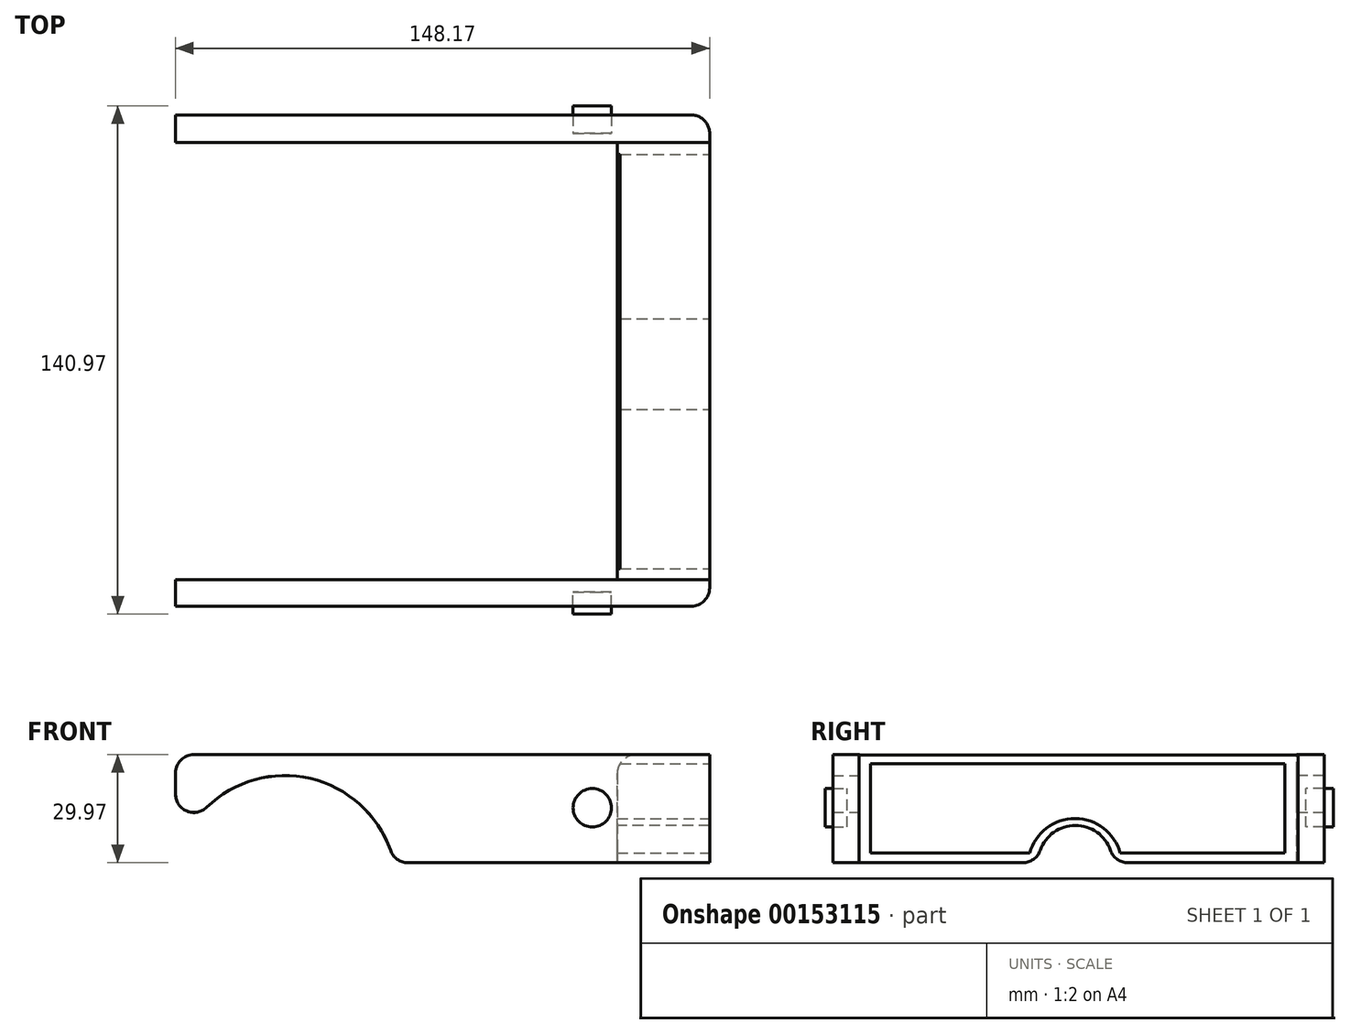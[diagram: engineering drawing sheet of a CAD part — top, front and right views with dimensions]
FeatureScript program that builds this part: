
annotation { "Feature Type Name" : "Feature", "Feature Type Description" : "" }
export const myFeature = defineFeature(function(context is Context, id is Id, definition is map)
    precondition{}
    {
        {
            var Q0;
            Q0=qCreatedBy(makeId("Front.planeOp"),FACE);
            var sketch = newSketch(context, id + "F0", { "sketchPlane" : qUnion([Q0])});
            skLineSegment(sketch, "E0", {"start": v(128.49, 29.97) * mm, "end": v(128.49, 0) * mm});
            skLineSegment(sketch, "E1", {"start": v(-19.65, 0) * mm, "end": v(-19.65, 29.97) * mm});
            skLineSegment(sketch, "E2", {"start": v(-19.65, 29.97) * mm, "end": v(128.49, 29.97) * mm});
            skArc(sketch, "E3", {"start": v(40.96, 0) * mm, "mid": v(10.65, 24.17) * mm, "end": v(-19.65, 0) * mm});
            skLineSegment(sketch, "E4", {"start": v(40.96, 0) * mm, "end": v(128.49, 0) * mm});
            skSolve(sketch);
        }
        {
            var Q0;
            Q0 = qSketchRegion(id + "F0", true);
            extrude(context, id + "F1", {"entities" : qUnion([Q0]), "depth" : 57.53 * mm, "hasSecondDirection" : true, "secondDirectionOppositeDirection" : false, "secondDirectionDepth" : 50.16 * mm});
        }
        {
            var Q0;
            Q0=qCreatedBy(makeId("Right.planeOp"),FACE);
            var sketch = newSketch(context, id + "F2", { "sketchPlane" : qUnion([Q0])});
            skLineSegment(sketch, "E5", {"start": v(-50.22, 29.87) * mm, "end": v(71.57, 29.87) * mm});
            skLineSegment(sketch, "E6", {"start": v(71.57, 29.87) * mm, "end": v(71.57, 0) * mm});
            skLineSegment(sketch, "E7", {"start": v(-50.22, 29.87) * mm, "end": v(-50.22, 0) * mm});
            skLineSegment(sketch, "E8", {"start": v(-50.22, 0) * mm, "end": v(-0.6, 0) * mm});
            skLineSegment(sketch, "E9", {"start": v(71.57, 0) * mm, "end": v(20.08, 0) * mm});
            skArc(sketch, "E10", {"start": v(20.08, 0) * mm, "mid": v(9.74, 10.34) * mm, "end": v(-0.6, 0) * mm});
            skSolve(sketch);
        }
        {
            var Q0;
            Q0 = qSketchRegion(id + "F2", true);
            extrude(context, id + "F3", {"entities" : qUnion([Q0]), "operationType" : NewBodyOperationType.ADD, "depth" : 128.52 * mm, "hasSecondDirection" : true, "secondDirectionOppositeDirection" : false, "secondDirectionDepth" : 102.87 * mm});
        }
        {
            var Q0;
            Q0=qCreatedBy(makeId("Right.planeOp"),FACE);
            var sketch = newSketch(context, id + "F4", { "sketchPlane" : qUnion([Q0])});
            skLineSegment(sketch, "E11", {"start": v(-47.14, 27.49) * mm, "end": v(-47.14, 2.64) * mm});
            skLineSegment(sketch, "E12", {"start": v(-47.14, 2.64) * mm, "end": v(-2.9, 2.64) * mm});
            skLineSegment(sketch, "E13", {"start": v(-47.14, 27.49) * mm, "end": v(67.8, 27.49) * mm});
            skLineSegment(sketch, "E14", {"start": v(67.8, 27.49) * mm, "end": v(67.8, 2.64) * mm});
            skLineSegment(sketch, "E15", {"start": v(67.8, 2.64) * mm, "end": v(22.17, 2.64) * mm});
            skArc(sketch, "E16", {"start": v(22.17, 2.64) * mm, "mid": v(9.63, 12.26) * mm, "end": v(-2.9, 2.64) * mm});
            skSolve(sketch);
        }
        {
            var Q0;
            Q0 = qSketchRegion(id + "F4", true);
            extrude(context, id + "F5", {"entities" : qUnion([Q0]), "operationType" : NewBodyOperationType.REMOVE, "oppositeDirection" : true, "depth" : 156.84 * mm, "hasSecondDirection" : true, "secondDirectionOppositeDirection" : false, "secondDirectionDepth" : 153.67 * mm});
        }
        {
            var Q0;
            Q0=makeQuery(id+"F1.opExtrude","CAP_FACE",FACE,{"disambiguationData":[OSD([sQuery(id+"F0.wireOp",EDGE,"t2ablPFP-ZTGi-keRe-My67-G8U3jhICAmQZ"),sQuery(id+"F0.wireOp",EDGE,"E0"),sQuery(id+"F0.wireOp",EDGE,"AoyKm1Ku-ZIaB-Dyan-j7dL-eiOp278ySbaL"),sQuery(id+"F0.wireOp",EDGE,"k48o5jMi-lDpC-vDEB-Jfvg-DJJhGkoViYC2"),sQuery(id+"F0.wireOp",EDGE,"NTX02WsM-8lT9-VH5H-J8AH-7PksFvNlZK1f")])],"isStart":true});
            var sketch = newSketch(context, id + "F6", { "sketchPlane" : qUnion([Q0])});
            skArc(sketch, "E17", {"start": v(19.65, 0) * mm, "mid": v(-10.65, 24.15) * mm, "end": v(-40.96, 0) * mm});
            skLineSegment(sketch, "E18", {"start": v(-40.96, 0) * mm, "end": v(-128.43, 0) * mm});
            skLineSegment(sketch, "E19", {"start": v(-128.43, 0) * mm, "end": v(-128.49, 29.97) * mm});
            skLineSegment(sketch, "E20", {"start": v(-128.49, 29.97) * mm, "end": v(19.65, 29.97) * mm});
            skLineSegment(sketch, "E21", {"start": v(19.65, 29.97) * mm, "end": v(19.65, 0) * mm});
            skSolve(sketch);
        }
        {
            var Q0;
            Q0 = qSketchRegion(id + "F6", true);
            extrude(context, id + "F7", {"entities" : qUnion([Q0]), "operationType" : NewBodyOperationType.ADD, "depth" : 128.9 * mm, "hasSecondDirection" : true, "secondDirectionOppositeDirection" : false, "secondDirectionDepth" : 121.28 * mm});
        }
        {
            var Q0;
            Q0=makeQuery(id+"F1.opExtrude","CAP_FACE",FACE,{"disambiguationData":[OSD([sQuery(id+"F0.wireOp",EDGE,"t2ablPFP-ZTGi-keRe-My67-G8U3jhICAmQZ"),sQuery(id+"F0.wireOp",EDGE,"E0"),sQuery(id+"F0.wireOp",EDGE,"AoyKm1Ku-ZIaB-Dyan-j7dL-eiOp278ySbaL"),sQuery(id+"F0.wireOp",EDGE,"k48o5jMi-lDpC-vDEB-Jfvg-DJJhGkoViYC2"),sQuery(id+"F0.wireOp",EDGE,"NTX02WsM-8lT9-VH5H-J8AH-7PksFvNlZK1f")])],"isStart":false});
            var sketch = newSketch(context, id + "F8", { "sketchPlane" : qUnion([Q0])});
            skCircle(sketch, "E22", {"center": v(95.95, 15.21) * mm, "radius": 5.33 * mm});
            skSolve(sketch);
        }
        {
            var Q0;
            Q0 = qSketchRegion(id + "F8", true);
            extrude(context, id + "F9", {"entities" : qUnion([Q0]), "depth" : 2.16 * mm, "hasSecondDirection" : true, "secondDirectionOppositeDirection" : true, "secondDirectionDepth" : 3.94 * mm});
        }
        {
            var Q0;
            Q0=makeQuery(id+"F9.opExtrude","CAP_FACE",FACE,{"disambiguationData":[OSD([sQuery(id+"F8.wireOp",EDGE,"E22")])],"isStart":false});
            var sketch = newSketch(context, id + "F10", { "sketchPlane" : qUnion([Q0])});
            skCircle(sketch, "E23", {"center": v(95.95, 15.21) * mm, "radius": 5.34 * mm});
            skSolve(sketch);
        }
        {
            var Q0;
            Q0 = qSketchRegion(id + "F10", true);
            extrude(context, id + "F11", {"entities" : qUnion([Q0]), "oppositeDirection" : true, "depth" : 140.97 * mm, "hasSecondDirection" : true, "secondDirectionOppositeDirection" : true, "secondDirectionDepth" : 133.35 * mm});
        }
        {
            var Q0;
            Q0=makeQuery(id+"F1.opExtrude","SWEPT_EDGE",EDGE,{"disambiguationData":[OSD([sQuery(id+"F0.wireOp",EDGE,"E1"),sQuery(id+"F0.wireOp",EDGE,"E3")])]});
            var Q1;
            Q1=makeQuery(id+"F7.opExtrude","SWEPT_EDGE",EDGE,{"disambiguationData":[OSD([sQuery(id+"F0.wireOp",EDGE,"E3"),sQuery(id+"F6.wireOp",EDGE,"E17"),sQuery(id+"F6.wireOp",EDGE,"E21")])]});
            var Q2;
            Q2=makeQuery(id+"F1.opExtrude","SWEPT_EDGE",EDGE,{"disambiguationData":[OSD([sQuery(id+"F0.wireOp",EDGE,"E1"),sQuery(id+"F0.wireOp",EDGE,"E2")])]});
            var Q3;
            Q3=makeQuery(id+"F7.opExtrude","SWEPT_EDGE",EDGE,{"disambiguationData":[OSD([sQuery(id+"F6.wireOp",EDGE,"E20"),sQuery(id+"F6.wireOp",EDGE,"E21")])]});
            fillet(context, id + "F12", {"entities" : qUnion([Q0, Q1, Q2, Q3]), "radius" : 5.08 * mm, "tangentPropagation" : true, "allowEdgeOverflow" : false});
        }
        {
            var Q0;
            Q0=makeQuery(id+"F1.opExtrude","SWEPT_EDGE",EDGE,{"disambiguationData":[OSD([sQuery(id+"F0.wireOp",EDGE,"E3"),sQuery(id+"F0.wireOp",EDGE,"E4")])]});
            var Q1;
            Q1=makeQuery(id+"F7.opExtrude","SWEPT_EDGE",EDGE,{"disambiguationData":[OSD([sQuery(id+"F0.wireOp",EDGE,"E3"),sQuery(id+"F6.wireOp",EDGE,"E17"),sQuery(id+"F6.wireOp",EDGE,"E18")])]});
            fillet(context, id + "F13", {"entities" : qUnion([Q0, Q1]), "radius" : 5.08 * mm, "tangentPropagation" : true, "allowEdgeOverflow" : false});
        }
        {
            var Q0;
            Q0=makeQuery(id+"F3.opExtrude","SWEPT_EDGE",EDGE,{"disambiguationData":[OSD([sQuery(id+"F2.wireOp",EDGE,"E8"),sQuery(id+"F2.wireOp",EDGE,"E10")])]});
            var Q1;
            Q1=makeQuery(id+"F3.opExtrude","SWEPT_EDGE",EDGE,{"disambiguationData":[OSD([sQuery(id+"F2.wireOp",EDGE,"E9"),sQuery(id+"F2.wireOp",EDGE,"E10")])]});
            fillet(context, id + "F14", {"entities" : qUnion([Q0, Q1]), "radius" : 5.08 * mm, "tangentPropagation" : true, "allowEdgeOverflow" : false});
        }
        {
            var Q0;
            Q0=makeQuery(id+"F7.boolean.opBoolean","SPLIT",EDGE,{"derivedFrom":makeQuery(id+"F3.opExtrude","CAP_EDGE",EDGE,{"disambiguationData":[OSD([sQuery(id+"F2.wireOp",EDGE,"E5")])],"isStart":true})});
            fillet(context, id + "F15", {"entities" : qUnion([Q0]), "radius" : 5.08 * mm, "tangentPropagation" : true, "allowEdgeOverflow" : false});
        }
        {
            var Q0;
            Q0=makeQuery(id+"F7.opExtrude","CAP_EDGE",EDGE,{"disambiguationData":[OSD([sQuery(id+"F6.wireOp",EDGE,"E19")])],"isStart":false});
            var Q1;
            Q1=makeQuery(id+"F1.opExtrude","CAP_EDGE",EDGE,{"disambiguationData":[OSD([sQuery(id+"F0.wireOp",EDGE,"E0")])],"isStart":false});
            fillet(context, id + "F16", {"entities" : qUnion([Q0, Q1]), "radius" : 5.08 * mm, "tangentPropagation" : true, "allowEdgeOverflow" : false});
        }
    });
